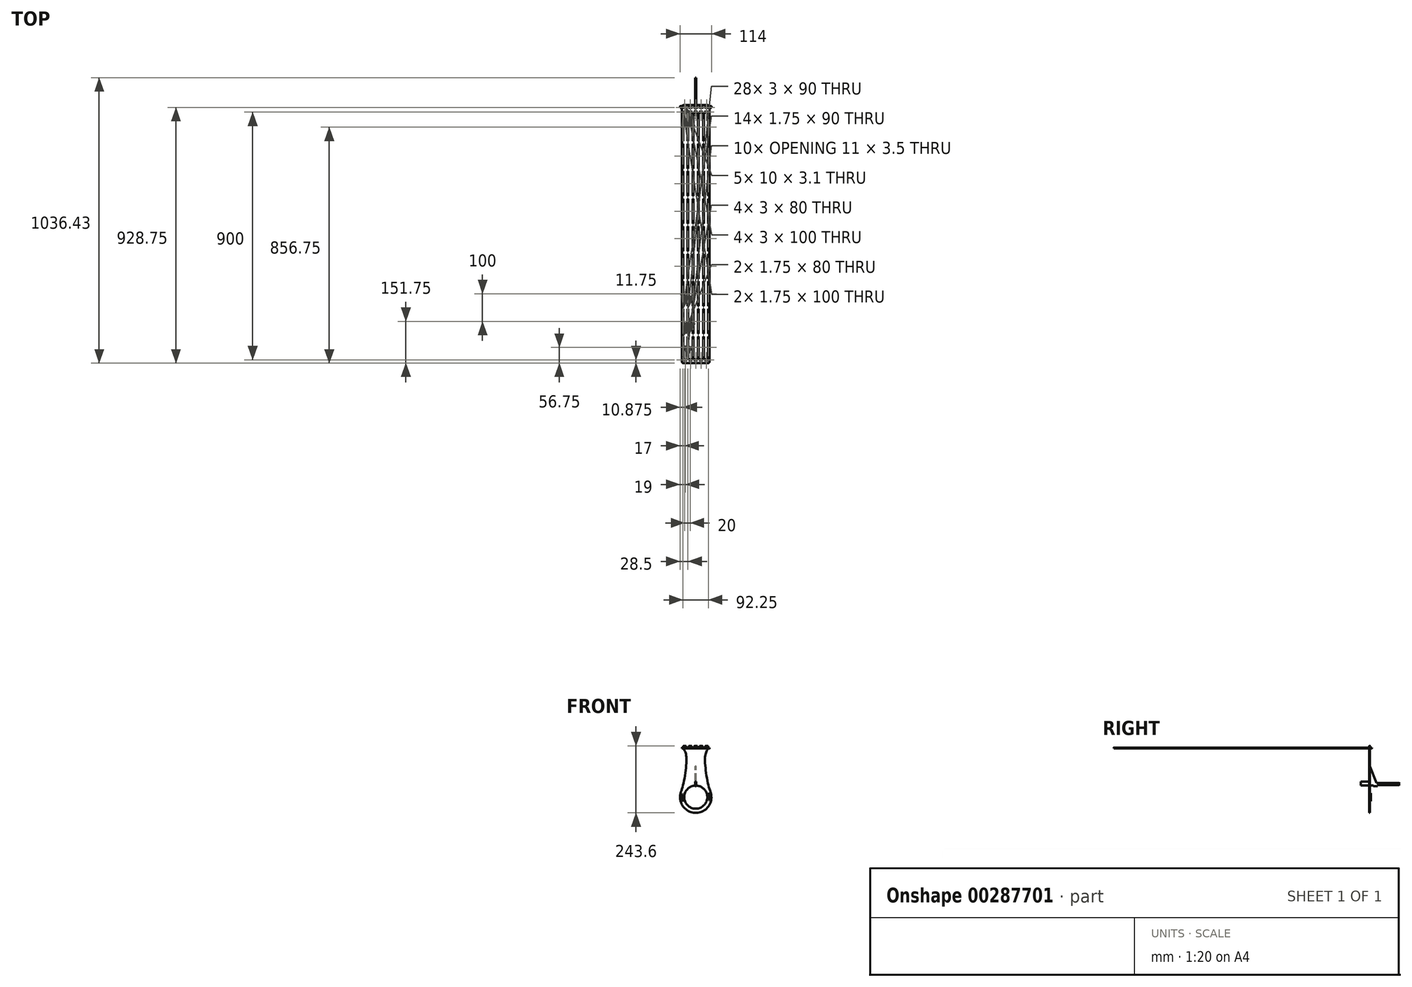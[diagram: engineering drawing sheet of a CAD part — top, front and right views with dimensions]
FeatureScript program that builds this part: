
annotation { "Feature Type Name" : "Feature", "Feature Type Description" : "" }
export const myFeature = defineFeature(function(context is Context, id is Id, definition is map)
    precondition{}
    {
        {
            var Q0;
            Q0=qCreatedBy(makeId("Top.planeOp"),FACE);
            var sketch = newSketch(context, id + "F0", { "sketchPlane" : qUnion([Q0])});
            skLineSegment(sketch, "E0.bottom", {"start": v(-45, 475) * mm, "end": v(45, 475) * mm});
            skLineSegment(sketch, "E0.top", {"start": v(-45, -475) * mm, "end": v(45, -475) * mm});
            skLineSegment(sketch, "E0.left", {"start": v(-50, 470) * mm, "end": v(-50, -456.75) * mm});
            skLineSegment(sketch, "E0.right", {"start": v(50, 470) * mm, "end": v(50, -456.75) * mm});
            skPoint(sketch, "E0.middle", {"position": v(0, 0) * mm});
            skLineSegment(sketch, "E1", {"start": v(-50, 450) * mm, "end": v(50, 450) * mm, "construction": true});
            skLineSegment(sketch, "E2", {"start": v(-50, -450) * mm, "end": v(50, -450) * mm, "construction": true});
            skLineSegment(sketch, "E3.bottom", {"start": v(-5, 451.75) * mm, "end": v(5, 451.75) * mm});
            skLineSegment(sketch, "E3.top", {"start": v(-5, 448.25) * mm, "end": v(5, 448.25) * mm});
            skLineSegment(sketch, "E3.left", {"start": v(-5.5, 451.25) * mm, "end": v(-5.5, 448.75) * mm});
            skLineSegment(sketch, "E3.right", {"start": v(5.5, 451.25) * mm, "end": v(5.5, 448.75) * mm});
            skPoint(sketch, "E3.middle", {"position": v(0, 450) * mm});
            skPoint(sketch, "E4.visualSharp", {"position": v(-5.5, 451.75) * mm});
            skArc(sketch, "E4.filletArc", {"start": v(-5, 451.75) * mm, "mid": v(-5.35, 451.6) * mm, "end": v(-5.5, 451.25) * mm});
            skPoint(sketch, "E5.visualSharp", {"position": v(-5.5, 448.25) * mm});
            skArc(sketch, "E5.filletArc", {"start": v(-5.5, 448.75) * mm, "mid": v(-5.35, 448.4) * mm, "end": v(-5, 448.25) * mm});
            skPoint(sketch, "E6.visualSharp", {"position": v(5.5, 451.75) * mm});
            skArc(sketch, "E6.filletArc", {"start": v(5.5, 451.25) * mm, "mid": v(5.35, 451.6) * mm, "end": v(5, 451.75) * mm});
            skPoint(sketch, "E7.visualSharp", {"position": v(5.5, 448.25) * mm});
            skArc(sketch, "E7.filletArc", {"start": v(5, 448.25) * mm, "mid": v(5.35, 448.4) * mm, "end": v(5.5, 448.75) * mm});
            skLineSegment(sketch, "E8.1.0.0", {"start": v(14, 451.75) * mm, "end": v(24, 451.75) * mm});
            skLineSegment(sketch, "E8.1.0.1", {"start": v(24.5, 451.25) * mm, "end": v(24.5, 448.75) * mm});
            skLineSegment(sketch, "E8.1.0.2", {"start": v(13.5, 451.25) * mm, "end": v(13.5, 448.75) * mm});
            skLineSegment(sketch, "E8.1.0.3", {"start": v(14, 448.25) * mm, "end": v(24, 448.25) * mm});
            skPoint(sketch, "E8.1.0.4", {"position": v(13.5, 448.25) * mm});
            skPoint(sketch, "E8.1.0.5", {"position": v(24.5, 451.75) * mm});
            skPoint(sketch, "E8.1.0.6", {"position": v(19, 450) * mm});
            skPoint(sketch, "E8.1.0.7", {"position": v(24.5, 448.25) * mm});
            skPoint(sketch, "E8.1.0.8", {"position": v(13.5, 451.75) * mm});
            skArc(sketch, "E8.1.0.9", {"start": v(24, 448.25) * mm, "mid": v(24.35, 448.4) * mm, "end": v(24.5, 448.75) * mm});
            skArc(sketch, "E8.1.0.10", {"start": v(14, 451.75) * mm, "mid": v(13.65, 451.6) * mm, "end": v(13.5, 451.25) * mm});
            skArc(sketch, "E8.1.0.11", {"start": v(13.5, 448.75) * mm, "mid": v(13.65, 448.4) * mm, "end": v(14, 448.25) * mm});
            skArc(sketch, "E8.1.0.12", {"start": v(24.5, 451.25) * mm, "mid": v(24.35, 451.6) * mm, "end": v(24, 451.75) * mm});
            skLineSegment(sketch, "E8.2.0.0", {"start": v(33, 451.75) * mm, "end": v(43, 451.75) * mm});
            skLineSegment(sketch, "E8.2.0.1", {"start": v(43.5, 451.25) * mm, "end": v(43.5, 448.75) * mm});
            skLineSegment(sketch, "E8.2.0.2", {"start": v(32.5, 451.25) * mm, "end": v(32.5, 448.75) * mm});
            skLineSegment(sketch, "E8.2.0.3", {"start": v(33, 448.25) * mm, "end": v(43, 448.25) * mm});
            skPoint(sketch, "E8.2.0.4", {"position": v(32.5, 448.25) * mm});
            skPoint(sketch, "E8.2.0.5", {"position": v(43.5, 451.75) * mm});
            skPoint(sketch, "E8.2.0.6", {"position": v(38, 450) * mm});
            skPoint(sketch, "E8.2.0.7", {"position": v(43.5, 448.25) * mm});
            skPoint(sketch, "E8.2.0.8", {"position": v(32.5, 451.75) * mm});
            skArc(sketch, "E8.2.0.9", {"start": v(43, 448.25) * mm, "mid": v(43.35, 448.4) * mm, "end": v(43.5, 448.75) * mm});
            skArc(sketch, "E8.2.0.10", {"start": v(33, 451.75) * mm, "mid": v(32.65, 451.6) * mm, "end": v(32.5, 451.25) * mm});
            skArc(sketch, "E8.2.0.11", {"start": v(32.5, 448.75) * mm, "mid": v(32.65, 448.4) * mm, "end": v(33, 448.25) * mm});
            skArc(sketch, "E8.2.0.12", {"start": v(43.5, 451.25) * mm, "mid": v(43.35, 451.6) * mm, "end": v(43, 451.75) * mm});
            skLineSegment(sketch, "E8.direction1", {"start": v(-5.5, 448.25) * mm, "end": v(13.5, 448.25) * mm, "construction": true});
            skPoint(sketch, "E9.1.0.0", {"position": v(-24.5, 448.25) * mm});
            skPoint(sketch, "E9.1.0.1", {"position": v(-13.5, 448.25) * mm});
            skPoint(sketch, "E9.1.0.2", {"position": v(-19, 450) * mm});
            skPoint(sketch, "E9.1.0.3", {"position": v(-13.5, 451.75) * mm});
            skPoint(sketch, "E9.1.0.4", {"position": v(-24.5, 451.75) * mm});
            skLineSegment(sketch, "E9.1.0.5", {"start": v(-24, 451.75) * mm, "end": v(-14, 451.75) * mm});
            skLineSegment(sketch, "E9.1.0.6", {"start": v(-24, 448.25) * mm, "end": v(-14, 448.25) * mm});
            skLineSegment(sketch, "E9.1.0.7", {"start": v(-24.5, 451.25) * mm, "end": v(-24.5, 448.75) * mm});
            skLineSegment(sketch, "E9.1.0.8", {"start": v(-13.5, 451.25) * mm, "end": v(-13.5, 448.75) * mm});
            skArc(sketch, "E9.1.0.9", {"start": v(-13.5, 451.25) * mm, "mid": v(-13.65, 451.6) * mm, "end": v(-14, 451.75) * mm});
            skArc(sketch, "E9.1.0.10", {"start": v(-24.5, 448.75) * mm, "mid": v(-24.35, 448.4) * mm, "end": v(-24, 448.25) * mm});
            skArc(sketch, "E9.1.0.11", {"start": v(-24, 451.75) * mm, "mid": v(-24.35, 451.6) * mm, "end": v(-24.5, 451.25) * mm});
            skArc(sketch, "E9.1.0.12", {"start": v(-14, 448.25) * mm, "mid": v(-13.65, 448.4) * mm, "end": v(-13.5, 448.75) * mm});
            skPoint(sketch, "E9.2.0.0", {"position": v(-43.5, 448.25) * mm});
            skPoint(sketch, "E9.2.0.1", {"position": v(-32.5, 448.25) * mm});
            skPoint(sketch, "E9.2.0.2", {"position": v(-38, 450) * mm});
            skPoint(sketch, "E9.2.0.3", {"position": v(-32.5, 451.75) * mm});
            skPoint(sketch, "E9.2.0.4", {"position": v(-43.5, 451.75) * mm});
            skLineSegment(sketch, "E9.2.0.5", {"start": v(-43, 451.75) * mm, "end": v(-33, 451.75) * mm});
            skLineSegment(sketch, "E9.2.0.6", {"start": v(-43, 448.25) * mm, "end": v(-33, 448.25) * mm});
            skLineSegment(sketch, "E9.2.0.7", {"start": v(-43.5, 451.25) * mm, "end": v(-43.5, 448.75) * mm});
            skLineSegment(sketch, "E9.2.0.8", {"start": v(-32.5, 451.25) * mm, "end": v(-32.5, 448.75) * mm});
            skArc(sketch, "E9.2.0.9", {"start": v(-32.5, 451.25) * mm, "mid": v(-32.65, 451.6) * mm, "end": v(-33, 451.75) * mm});
            skArc(sketch, "E9.2.0.10", {"start": v(-43.5, 448.75) * mm, "mid": v(-43.35, 448.4) * mm, "end": v(-43, 448.25) * mm});
            skArc(sketch, "E9.2.0.11", {"start": v(-43, 451.75) * mm, "mid": v(-43.35, 451.6) * mm, "end": v(-43.5, 451.25) * mm});
            skArc(sketch, "E9.2.0.12", {"start": v(-33, 448.25) * mm, "mid": v(-32.65, 448.4) * mm, "end": v(-32.5, 448.75) * mm});
            skLineSegment(sketch, "E9.direction1", {"start": v(-5.5, 448.25) * mm, "end": v(-24.5, 448.25) * mm, "construction": true});
            skLineSegment(sketch, "E10", {"start": v(-50, 467) * mm, "end": v(50, 467) * mm, "construction": true});
            skLineSegment(sketch, "E11.bottom", {"start": v(-5, 468.55) * mm, "end": v(5, 468.55) * mm});
            skLineSegment(sketch, "E11.top", {"start": v(-5, 465.45) * mm, "end": v(5, 465.45) * mm});
            skLineSegment(sketch, "E11.left", {"start": v(-5, 468.55) * mm, "end": v(-5, 465.45) * mm});
            skLineSegment(sketch, "E11.right", {"start": v(5, 468.55) * mm, "end": v(5, 465.45) * mm});
            skPoint(sketch, "E11.middle", {"position": v(0, 467) * mm});
            skPoint(sketch, "E12.visualSharp", {"position": v(-50, 475) * mm});
            skArc(sketch, "E12.filletArc", {"start": v(-45, 475) * mm, "mid": v(-48.54, 473.54) * mm, "end": v(-50, 470) * mm});
            skPoint(sketch, "E13.visualSharp", {"position": v(50, 475) * mm});
            skArc(sketch, "E13.filletArc", {"start": v(50, 470) * mm, "mid": v(48.54, 473.54) * mm, "end": v(45, 475) * mm});
            skPoint(sketch, "E14.visualSharp", {"position": v(-50, -475) * mm});
            skArc(sketch, "E14.filletArc", {"start": v(-50, -470) * mm, "mid": v(-48.54, -473.54) * mm, "end": v(-45, -475) * mm});
            skPoint(sketch, "E15.visualSharp", {"position": v(50, -475) * mm});
            skArc(sketch, "E15.filletArc", {"start": v(45, -475) * mm, "mid": v(48.54, -473.54) * mm, "end": v(50, -470) * mm});
            skPoint(sketch, "E16.1.0.0", {"position": v(20, 467) * mm});
            skLineSegment(sketch, "E16.1.0.1", {"start": v(25, 468.55) * mm, "end": v(25, 465.45) * mm});
            skLineSegment(sketch, "E16.1.0.2", {"start": v(15, 468.55) * mm, "end": v(25, 468.55) * mm});
            skLineSegment(sketch, "E16.1.0.3", {"start": v(15, 468.55) * mm, "end": v(15, 465.45) * mm});
            skLineSegment(sketch, "E16.1.0.4", {"start": v(15, 465.45) * mm, "end": v(25, 465.45) * mm});
            skPoint(sketch, "E16.2.0.0", {"position": v(40, 467) * mm});
            skLineSegment(sketch, "E16.2.0.1", {"start": v(45, 468.55) * mm, "end": v(45, 465.45) * mm});
            skLineSegment(sketch, "E16.2.0.2", {"start": v(35, 468.55) * mm, "end": v(45, 468.55) * mm});
            skLineSegment(sketch, "E16.2.0.3", {"start": v(35, 468.55) * mm, "end": v(35, 465.45) * mm});
            skLineSegment(sketch, "E16.2.0.4", {"start": v(35, 465.45) * mm, "end": v(45, 465.45) * mm});
            skLineSegment(sketch, "E16.direction1", {"start": v(-5, 465.45) * mm, "end": v(15, 465.45) * mm, "construction": true});
            skLineSegment(sketch, "E17.1.0.0", {"start": v(-15, 468.55) * mm, "end": v(-15, 465.45) * mm});
            skLineSegment(sketch, "E17.1.0.1", {"start": v(-25, 468.55) * mm, "end": v(-25, 465.45) * mm});
            skPoint(sketch, "E17.1.0.2", {"position": v(-20, 467) * mm});
            skLineSegment(sketch, "E17.1.0.3", {"start": v(-25, 465.45) * mm, "end": v(-15, 465.45) * mm});
            skLineSegment(sketch, "E17.1.0.4", {"start": v(-25, 468.55) * mm, "end": v(-15, 468.55) * mm});
            skLineSegment(sketch, "E17.2.0.0", {"start": v(-35, 468.55) * mm, "end": v(-35, 465.45) * mm});
            skLineSegment(sketch, "E17.2.0.1", {"start": v(-45, 468.55) * mm, "end": v(-45, 465.45) * mm});
            skPoint(sketch, "E17.2.0.2", {"position": v(-40, 467) * mm});
            skLineSegment(sketch, "E17.2.0.3", {"start": v(-45, 465.45) * mm, "end": v(-35, 465.45) * mm});
            skLineSegment(sketch, "E17.2.0.4", {"start": v(-45, 468.55) * mm, "end": v(-35, 468.55) * mm});
            skLineSegment(sketch, "E17.direction1", {"start": v(-5, 465.45) * mm, "end": v(-25, 465.45) * mm, "construction": true});
            skArc(sketch, "E18.MirrorCS", {"start": v(-5.5, -448.75) * mm, "mid": v(-5.35, -448.4) * mm, "end": v(-5, -448.25) * mm});
            skArc(sketch, "E19.MirrorCS", {"start": v(24, -448.25) * mm, "mid": v(24.35, -448.4) * mm, "end": v(24.5, -448.75) * mm});
            skArc(sketch, "E20.MirrorCS", {"start": v(5.5, -451.25) * mm, "mid": v(5.35, -451.6) * mm, "end": v(5, -451.75) * mm});
            skArc(sketch, "E21.MirrorCS", {"start": v(-5, -451.75) * mm, "mid": v(-5.35, -451.6) * mm, "end": v(-5.5, -451.25) * mm});
            skArc(sketch, "E22.MirrorCS", {"start": v(5, -448.25) * mm, "mid": v(5.35, -448.4) * mm, "end": v(5.5, -448.75) * mm});
            skArc(sketch, "E23.MirrorCS", {"start": v(-14, -448.25) * mm, "mid": v(-13.65, -448.4) * mm, "end": v(-13.5, -448.75) * mm});
            skArc(sketch, "E24.MirrorCS", {"start": v(-24, -451.75) * mm, "mid": v(-24.35, -451.6) * mm, "end": v(-24.5, -451.25) * mm});
            skArc(sketch, "E25.MirrorCS", {"start": v(-33, -448.25) * mm, "mid": v(-32.65, -448.4) * mm, "end": v(-32.5, -448.75) * mm});
            skArc(sketch, "E26.MirrorCS", {"start": v(24.5, -451.25) * mm, "mid": v(24.35, -451.6) * mm, "end": v(24, -451.75) * mm});
            skArc(sketch, "E27.MirrorCS", {"start": v(32.5, -448.75) * mm, "mid": v(32.65, -448.4) * mm, "end": v(33, -448.25) * mm});
            skArc(sketch, "E28.MirrorCS", {"start": v(-43.5, -448.75) * mm, "mid": v(-43.35, -448.4) * mm, "end": v(-43, -448.25) * mm});
            skArc(sketch, "E29.MirrorCS", {"start": v(-24.5, -448.75) * mm, "mid": v(-24.35, -448.4) * mm, "end": v(-24, -448.25) * mm});
            skArc(sketch, "E30.MirrorCS", {"start": v(43.5, -451.25) * mm, "mid": v(43.35, -451.6) * mm, "end": v(43, -451.75) * mm});
            skArc(sketch, "E31.MirrorCS", {"start": v(-43, -451.75) * mm, "mid": v(-43.35, -451.6) * mm, "end": v(-43.5, -451.25) * mm});
            skArc(sketch, "E32.MirrorCS", {"start": v(13.5, -448.75) * mm, "mid": v(13.65, -448.4) * mm, "end": v(14, -448.25) * mm});
            skArc(sketch, "E33.MirrorCS", {"start": v(33, -451.75) * mm, "mid": v(32.65, -451.6) * mm, "end": v(32.5, -451.25) * mm});
            skArc(sketch, "E34.MirrorCS", {"start": v(-32.5, -451.25) * mm, "mid": v(-32.65, -451.6) * mm, "end": v(-33, -451.75) * mm});
            skArc(sketch, "E35.MirrorCS", {"start": v(-13.5, -451.25) * mm, "mid": v(-13.65, -451.6) * mm, "end": v(-14, -451.75) * mm});
            skArc(sketch, "E36.MirrorCS", {"start": v(14, -451.75) * mm, "mid": v(13.65, -451.6) * mm, "end": v(13.5, -451.25) * mm});
            skArc(sketch, "E37.MirrorCS", {"start": v(43, -448.25) * mm, "mid": v(43.35, -448.4) * mm, "end": v(43.5, -448.75) * mm});
            skLineSegment(sketch, "E38.MirrorCS", {"start": v(-13.5, -451.25) * mm, "end": v(-13.5, -448.75) * mm});
            skLineSegment(sketch, "E39.MirrorCS", {"start": v(-24, -448.25) * mm, "end": v(-14, -448.25) * mm});
            skLineSegment(sketch, "E40.MirrorCS", {"start": v(-5, -448.25) * mm, "end": v(5, -448.25) * mm});
            skPoint(sketch, "E41.MirrorP", {"position": v(32.5, -448.25) * mm});
            skLineSegment(sketch, "E42.MirrorCS", {"start": v(33, -448.25) * mm, "end": v(43, -448.25) * mm});
            skLineSegment(sketch, "E43.MirrorCS", {"start": v(-43.5, -451.25) * mm, "end": v(-43.5, -448.75) * mm});
            skPoint(sketch, "E44.MirrorP", {"position": v(19, -450) * mm});
            skPoint(sketch, "E45.MirrorP", {"position": v(-24.5, -448.25) * mm});
            skPoint(sketch, "E46.MirrorP", {"position": v(-5.5, -451.75) * mm});
            skLineSegment(sketch, "E47.MirrorCS", {"start": v(-24.5, -451.25) * mm, "end": v(-24.5, -448.75) * mm});
            skLineSegment(sketch, "E48.MirrorCS", {"start": v(14, -448.25) * mm, "end": v(24, -448.25) * mm});
            skPoint(sketch, "E49.MirrorP", {"position": v(24.5, -451.75) * mm});
            skLineSegment(sketch, "E50.MirrorCS", {"start": v(32.5, -451.25) * mm, "end": v(32.5, -448.75) * mm});
            skLineSegment(sketch, "E51.MirrorCS", {"start": v(-43, -448.25) * mm, "end": v(-33, -448.25) * mm});
            skLineSegment(sketch, "E52.MirrorCS", {"start": v(13.5, -451.25) * mm, "end": v(13.5, -448.75) * mm});
            skPoint(sketch, "E53.MirrorP", {"position": v(13.5, -448.25) * mm});
            skLineSegment(sketch, "E54.MirrorCS", {"start": v(43.5, -451.25) * mm, "end": v(43.5, -448.75) * mm});
            skLineSegment(sketch, "E55.MirrorCS", {"start": v(-43, -451.75) * mm, "end": v(-33, -451.75) * mm});
            skPoint(sketch, "E56.MirrorP", {"position": v(0, -450) * mm});
            skLineSegment(sketch, "E57.MirrorCS", {"start": v(5.5, -451.25) * mm, "end": v(5.5, -448.75) * mm});
            skLineSegment(sketch, "E58.MirrorCS", {"start": v(-5.5, -451.25) * mm, "end": v(-5.5, -448.75) * mm});
            skLineSegment(sketch, "E59.MirrorCS", {"start": v(-5, -451.75) * mm, "end": v(5, -451.75) * mm});
            skLineSegment(sketch, "E60.MirrorCS", {"start": v(24.5, -451.25) * mm, "end": v(24.5, -448.75) * mm});
            skLineSegment(sketch, "E61.MirrorCS", {"start": v(14, -451.75) * mm, "end": v(24, -451.75) * mm});
            skLineSegment(sketch, "E62.MirrorCS", {"start": v(-24, -451.75) * mm, "end": v(-14, -451.75) * mm});
            skLineSegment(sketch, "E63.MirrorCS", {"start": v(-5.5, -448.25) * mm, "end": v(-24.5, -448.25) * mm, "construction": true});
            skLineSegment(sketch, "E64.MirrorCS", {"start": v(33, -451.75) * mm, "end": v(43, -451.75) * mm});
            skPoint(sketch, "E65.MirrorP", {"position": v(-24.5, -451.75) * mm});
            skPoint(sketch, "E66.MirrorP", {"position": v(-43.5, -451.75) * mm});
            skPoint(sketch, "E67.MirrorP", {"position": v(-32.5, -448.25) * mm});
            skPoint(sketch, "E68.MirrorP", {"position": v(5.5, -451.75) * mm});
            skPoint(sketch, "E69.MirrorP", {"position": v(43.5, -448.25) * mm});
            skLineSegment(sketch, "E70.MirrorCS", {"start": v(-5.5, -448.25) * mm, "end": v(13.5, -448.25) * mm, "construction": true});
            skPoint(sketch, "E71.MirrorP", {"position": v(5.5, -448.25) * mm});
            skPoint(sketch, "E72.MirrorP", {"position": v(-13.5, -451.75) * mm});
            skPoint(sketch, "E73.MirrorP", {"position": v(-32.5, -451.75) * mm});
            skPoint(sketch, "E74.MirrorP", {"position": v(-43.5, -448.25) * mm});
            skPoint(sketch, "E75.MirrorP", {"position": v(38, -450) * mm});
            skPoint(sketch, "E76.MirrorP", {"position": v(13.5, -451.75) * mm});
            skPoint(sketch, "E77.MirrorP", {"position": v(32.5, -451.75) * mm});
            skPoint(sketch, "E78.MirrorP", {"position": v(-19, -450) * mm});
            skPoint(sketch, "E79.MirrorP", {"position": v(-38, -450) * mm});
            skPoint(sketch, "E80.MirrorP", {"position": v(-5.5, -448.25) * mm});
            skPoint(sketch, "E81.MirrorP", {"position": v(43.5, -451.75) * mm});
            skLineSegment(sketch, "E82.MirrorCS", {"start": v(-32.5, -451.25) * mm, "end": v(-32.5, -448.75) * mm});
            skPoint(sketch, "E83.MirrorP", {"position": v(24.5, -448.25) * mm});
            skPoint(sketch, "E84.MirrorP", {"position": v(-13.5, -448.25) * mm});
            skLineSegment(sketch, "E85", {"start": v(-45, -461.75) * mm, "end": v(45, -461.75) * mm});
            skArc(sketch, "E86.filletArc", {"start": v(-50, -456.75) * mm, "mid": v(-48.54, -460.29) * mm, "end": v(-45, -461.75) * mm});
            skArc(sketch, "E87.filletArc", {"start": v(45, -461.75) * mm, "mid": v(48.54, -460.29) * mm, "end": v(50, -456.75) * mm});
            skLineSegment(sketch, "E88.bottom", {"start": v(-30, 445) * mm, "end": v(-27, 445) * mm});
            skLineSegment(sketch, "E88.top", {"start": v(-30, -445) * mm, "end": v(-27, -445) * mm});
            skLineSegment(sketch, "E88.left", {"start": v(-30, 445) * mm, "end": v(-30, -445) * mm});
            skLineSegment(sketch, "E88.right", {"start": v(-27, 445) * mm, "end": v(-27, -445) * mm});
            skLineSegment(sketch, "E89.1.0.0", {"start": v(-11, 445) * mm, "end": v(-11, -445) * mm});
            skLineSegment(sketch, "E89.1.0.1", {"start": v(-11, 445) * mm, "end": v(-8, 445) * mm});
            skLineSegment(sketch, "E89.1.0.2", {"start": v(-8, 445) * mm, "end": v(-8, -445) * mm});
            skLineSegment(sketch, "E89.1.0.3", {"start": v(-11, -445) * mm, "end": v(-8, -445) * mm});
            skLineSegment(sketch, "E89.2.0.0", {"start": v(8, 445) * mm, "end": v(8, -445) * mm});
            skLineSegment(sketch, "E89.2.0.1", {"start": v(8, 445) * mm, "end": v(11, 445) * mm});
            skLineSegment(sketch, "E89.2.0.2", {"start": v(11, 445) * mm, "end": v(11, -445) * mm});
            skLineSegment(sketch, "E89.2.0.3", {"start": v(8, -445) * mm, "end": v(11, -445) * mm});
            skLineSegment(sketch, "E89.3.0.0", {"start": v(27, 445) * mm, "end": v(27, -445) * mm});
            skLineSegment(sketch, "E89.3.0.1", {"start": v(27, 445) * mm, "end": v(30, 445) * mm});
            skLineSegment(sketch, "E89.3.0.2", {"start": v(30, 445) * mm, "end": v(30, -445) * mm});
            skLineSegment(sketch, "E89.3.0.3", {"start": v(27, -445) * mm, "end": v(30, -445) * mm});
            skLineSegment(sketch, "E89.direction1", {"start": v(-30, -445) * mm, "end": v(-11, -445) * mm, "construction": true});
            skLineSegment(sketch, "E90", {"start": v(-47, 445) * mm, "end": v(-45.25, 445) * mm});
            skLineSegment(sketch, "E91", {"start": v(-45.25, 445) * mm, "end": v(-45.25, -445) * mm});
            skLineSegment(sketch, "E92", {"start": v(-45.25, -445) * mm, "end": v(-47, -445) * mm});
            skLineSegment(sketch, "E93", {"start": v(-47, -445) * mm, "end": v(-47, 445) * mm});
            skLineSegment(sketch, "E94.MirrorCS", {"start": v(47, 445) * mm, "end": v(45.25, 445) * mm});
            skLineSegment(sketch, "E95.MirrorCS", {"start": v(47, -445) * mm, "end": v(47, 445) * mm});
            skLineSegment(sketch, "E96.MirrorCS", {"start": v(45.25, 445) * mm, "end": v(45.25, -445) * mm});
            skLineSegment(sketch, "E97.MirrorCS", {"start": v(45.25, -445) * mm, "end": v(47, -445) * mm});
            skLineSegment(sketch, "E98", {"start": v(-47, 345) * mm, "end": v(-45.25, 345) * mm});
            skLineSegment(sketch, "E99", {"start": v(-30, 345) * mm, "end": v(-27, 345) * mm});
            skLineSegment(sketch, "E100", {"start": v(-11, 345) * mm, "end": v(-8, 345) * mm});
            skLineSegment(sketch, "E101", {"start": v(8, 345) * mm, "end": v(11, 345) * mm});
            skLineSegment(sketch, "E102", {"start": v(27, 345) * mm, "end": v(30, 345) * mm});
            skLineSegment(sketch, "E103", {"start": v(45.25, 345) * mm, "end": v(47, 345) * mm});
            skLineSegment(sketch, "E104", {"start": v(-47, 335) * mm, "end": v(-45.25, 335) * mm});
            skLineSegment(sketch, "E105", {"start": v(-30, 335) * mm, "end": v(-27, 335) * mm});
            skLineSegment(sketch, "E106", {"start": v(-11, 335) * mm, "end": v(-8, 335) * mm});
            skLineSegment(sketch, "E107", {"start": v(8, 335) * mm, "end": v(11, 335) * mm});
            skLineSegment(sketch, "E108", {"start": v(27, 335) * mm, "end": v(30, 335) * mm});
            skLineSegment(sketch, "E109", {"start": v(45.25, 335) * mm, "end": v(47, 335) * mm});
            skLineSegment(sketch, "E110.0.1.0", {"start": v(-47, 245) * mm, "end": v(-45.25, 245) * mm});
            skLineSegment(sketch, "E110.0.1.1", {"start": v(-47, 235) * mm, "end": v(-45.25, 235) * mm});
            skLineSegment(sketch, "E110.0.1.2", {"start": v(-30, 245) * mm, "end": v(-27, 245) * mm});
            skLineSegment(sketch, "E110.0.1.3", {"start": v(-30, 235) * mm, "end": v(-27, 235) * mm});
            skLineSegment(sketch, "E110.0.1.4", {"start": v(-11, 245) * mm, "end": v(-8, 245) * mm});
            skLineSegment(sketch, "E110.0.1.5", {"start": v(-11, 235) * mm, "end": v(-8, 235) * mm});
            skLineSegment(sketch, "E110.0.1.6", {"start": v(8, 245) * mm, "end": v(11, 245) * mm});
            skLineSegment(sketch, "E110.0.1.7", {"start": v(8, 235) * mm, "end": v(11, 235) * mm});
            skLineSegment(sketch, "E110.0.1.8", {"start": v(27, 245) * mm, "end": v(30, 245) * mm});
            skLineSegment(sketch, "E110.0.1.9", {"start": v(27, 235) * mm, "end": v(30, 235) * mm});
            skLineSegment(sketch, "E110.0.1.10", {"start": v(45.25, 245) * mm, "end": v(47, 245) * mm});
            skLineSegment(sketch, "E110.0.1.11", {"start": v(45.25, 235) * mm, "end": v(47, 235) * mm});
            skLineSegment(sketch, "E110.0.2.0", {"start": v(-47, 145) * mm, "end": v(-45.25, 145) * mm});
            skLineSegment(sketch, "E110.0.2.1", {"start": v(-47, 135) * mm, "end": v(-45.25, 135) * mm});
            skLineSegment(sketch, "E110.0.2.2", {"start": v(-30, 145) * mm, "end": v(-27, 145) * mm});
            skLineSegment(sketch, "E110.0.2.3", {"start": v(-30, 135) * mm, "end": v(-27, 135) * mm});
            skLineSegment(sketch, "E110.0.2.4", {"start": v(-11, 145) * mm, "end": v(-8, 145) * mm});
            skLineSegment(sketch, "E110.0.2.5", {"start": v(-11, 135) * mm, "end": v(-8, 135) * mm});
            skLineSegment(sketch, "E110.0.2.6", {"start": v(8, 145) * mm, "end": v(11, 145) * mm});
            skLineSegment(sketch, "E110.0.2.7", {"start": v(8, 135) * mm, "end": v(11, 135) * mm});
            skLineSegment(sketch, "E110.0.2.8", {"start": v(27, 145) * mm, "end": v(30, 145) * mm});
            skLineSegment(sketch, "E110.0.2.9", {"start": v(27, 135) * mm, "end": v(30, 135) * mm});
            skLineSegment(sketch, "E110.0.2.10", {"start": v(45.25, 145) * mm, "end": v(47, 145) * mm});
            skLineSegment(sketch, "E110.0.2.11", {"start": v(45.25, 135) * mm, "end": v(47, 135) * mm});
            skLineSegment(sketch, "E110.0.3.0", {"start": v(-47, 45) * mm, "end": v(-45.25, 45) * mm});
            skLineSegment(sketch, "E110.0.3.1", {"start": v(-47, 35) * mm, "end": v(-45.25, 35) * mm});
            skLineSegment(sketch, "E110.0.3.2", {"start": v(-30, 45) * mm, "end": v(-27, 45) * mm});
            skLineSegment(sketch, "E110.0.3.3", {"start": v(-30, 35) * mm, "end": v(-27, 35) * mm});
            skLineSegment(sketch, "E110.0.3.4", {"start": v(-11, 45) * mm, "end": v(-8, 45) * mm});
            skLineSegment(sketch, "E110.0.3.5", {"start": v(-11, 35) * mm, "end": v(-8, 35) * mm});
            skLineSegment(sketch, "E110.0.3.6", {"start": v(8, 45) * mm, "end": v(11, 45) * mm});
            skLineSegment(sketch, "E110.0.3.7", {"start": v(8, 35) * mm, "end": v(11, 35) * mm});
            skLineSegment(sketch, "E110.0.3.8", {"start": v(27, 45) * mm, "end": v(30, 45) * mm});
            skLineSegment(sketch, "E110.0.3.9", {"start": v(27, 35) * mm, "end": v(30, 35) * mm});
            skLineSegment(sketch, "E110.0.3.10", {"start": v(45.25, 45) * mm, "end": v(47, 45) * mm});
            skLineSegment(sketch, "E110.0.3.11", {"start": v(45.25, 35) * mm, "end": v(47, 35) * mm});
            skLineSegment(sketch, "E110.0.4.0", {"start": v(-47, -55) * mm, "end": v(-45.25, -55) * mm});
            skLineSegment(sketch, "E110.0.4.1", {"start": v(-47, -65) * mm, "end": v(-45.25, -65) * mm});
            skLineSegment(sketch, "E110.0.4.2", {"start": v(-30, -55) * mm, "end": v(-27, -55) * mm});
            skLineSegment(sketch, "E110.0.4.3", {"start": v(-30, -65) * mm, "end": v(-27, -65) * mm});
            skLineSegment(sketch, "E110.0.4.4", {"start": v(-11, -55) * mm, "end": v(-8, -55) * mm});
            skLineSegment(sketch, "E110.0.4.5", {"start": v(-11, -65) * mm, "end": v(-8, -65) * mm});
            skLineSegment(sketch, "E110.0.4.6", {"start": v(8, -55) * mm, "end": v(11, -55) * mm});
            skLineSegment(sketch, "E110.0.4.7", {"start": v(8, -65) * mm, "end": v(11, -65) * mm});
            skLineSegment(sketch, "E110.0.4.8", {"start": v(27, -55) * mm, "end": v(30, -55) * mm});
            skLineSegment(sketch, "E110.0.4.9", {"start": v(27, -65) * mm, "end": v(30, -65) * mm});
            skLineSegment(sketch, "E110.0.4.10", {"start": v(45.25, -55) * mm, "end": v(47, -55) * mm});
            skLineSegment(sketch, "E110.0.4.11", {"start": v(45.25, -65) * mm, "end": v(47, -65) * mm});
            skLineSegment(sketch, "E110.0.5.0", {"start": v(-47, -155) * mm, "end": v(-45.25, -155) * mm});
            skLineSegment(sketch, "E110.0.5.1", {"start": v(-47, -165) * mm, "end": v(-45.25, -165) * mm});
            skLineSegment(sketch, "E110.0.5.2", {"start": v(-30, -155) * mm, "end": v(-27, -155) * mm});
            skLineSegment(sketch, "E110.0.5.3", {"start": v(-30, -165) * mm, "end": v(-27, -165) * mm});
            skLineSegment(sketch, "E110.0.5.4", {"start": v(-11, -155) * mm, "end": v(-8, -155) * mm});
            skLineSegment(sketch, "E110.0.5.5", {"start": v(-11, -165) * mm, "end": v(-8, -165) * mm});
            skLineSegment(sketch, "E110.0.5.6", {"start": v(8, -155) * mm, "end": v(11, -155) * mm});
            skLineSegment(sketch, "E110.0.5.7", {"start": v(8, -165) * mm, "end": v(11, -165) * mm});
            skLineSegment(sketch, "E110.0.5.8", {"start": v(27, -155) * mm, "end": v(30, -155) * mm});
            skLineSegment(sketch, "E110.0.5.9", {"start": v(27, -165) * mm, "end": v(30, -165) * mm});
            skLineSegment(sketch, "E110.0.5.10", {"start": v(45.25, -155) * mm, "end": v(47, -155) * mm});
            skLineSegment(sketch, "E110.0.5.11", {"start": v(45.25, -165) * mm, "end": v(47, -165) * mm});
            skLineSegment(sketch, "E110.0.6.0", {"start": v(-47, -255) * mm, "end": v(-45.25, -255) * mm});
            skLineSegment(sketch, "E110.0.6.1", {"start": v(-47, -265) * mm, "end": v(-45.25, -265) * mm});
            skLineSegment(sketch, "E110.0.6.2", {"start": v(-30, -255) * mm, "end": v(-27, -255) * mm});
            skLineSegment(sketch, "E110.0.6.3", {"start": v(-30, -265) * mm, "end": v(-27, -265) * mm});
            skLineSegment(sketch, "E110.0.6.4", {"start": v(-11, -255) * mm, "end": v(-8, -255) * mm});
            skLineSegment(sketch, "E110.0.6.5", {"start": v(-11, -265) * mm, "end": v(-8, -265) * mm});
            skLineSegment(sketch, "E110.0.6.6", {"start": v(8, -255) * mm, "end": v(11, -255) * mm});
            skLineSegment(sketch, "E110.0.6.7", {"start": v(8, -265) * mm, "end": v(11, -265) * mm});
            skLineSegment(sketch, "E110.0.6.8", {"start": v(27, -255) * mm, "end": v(30, -255) * mm});
            skLineSegment(sketch, "E110.0.6.9", {"start": v(27, -265) * mm, "end": v(30, -265) * mm});
            skLineSegment(sketch, "E110.0.6.10", {"start": v(45.25, -255) * mm, "end": v(47, -255) * mm});
            skLineSegment(sketch, "E110.0.6.11", {"start": v(45.25, -265) * mm, "end": v(47, -265) * mm});
            skLineSegment(sketch, "E110.0.7.0", {"start": v(-47, -355) * mm, "end": v(-45.25, -355) * mm});
            skLineSegment(sketch, "E110.0.7.1", {"start": v(-47, -365) * mm, "end": v(-45.25, -365) * mm});
            skLineSegment(sketch, "E110.0.7.2", {"start": v(-30, -355) * mm, "end": v(-27, -355) * mm});
            skLineSegment(sketch, "E110.0.7.3", {"start": v(-30, -365) * mm, "end": v(-27, -365) * mm});
            skLineSegment(sketch, "E110.0.7.4", {"start": v(-11, -355) * mm, "end": v(-8, -355) * mm});
            skLineSegment(sketch, "E110.0.7.5", {"start": v(-11, -365) * mm, "end": v(-8, -365) * mm});
            skLineSegment(sketch, "E110.0.7.6", {"start": v(8, -355) * mm, "end": v(11, -355) * mm});
            skLineSegment(sketch, "E110.0.7.7", {"start": v(8, -365) * mm, "end": v(11, -365) * mm});
            skLineSegment(sketch, "E110.0.7.8", {"start": v(27, -355) * mm, "end": v(30, -355) * mm});
            skLineSegment(sketch, "E110.0.7.9", {"start": v(27, -365) * mm, "end": v(30, -365) * mm});
            skLineSegment(sketch, "E110.0.7.10", {"start": v(45.25, -355) * mm, "end": v(47, -355) * mm});
            skLineSegment(sketch, "E110.0.7.11", {"start": v(45.25, -365) * mm, "end": v(47, -365) * mm});
            skLineSegment(sketch, "E110.direction1", {"start": v(-47, 335) * mm, "end": v(-22, 335) * mm, "construction": true});
            skLineSegment(sketch, "E110.direction2", {"start": v(-47, 335) * mm, "end": v(-47, 235) * mm, "construction": true});
            skSolve(sketch);
        }
        {
            var Q0;
            Q0=sQuery(id+"F0.wireOp",EDGE,"E11.top");
            cPlane(context, id + "F1", {"entities" : qUnion([Q0]), "cplaneType" : CPlaneType.LINE_ANGLE, "offset" : 25 * mm, "angle" : 0 * degree, "width" : 150 * mm, "height" : 150 * mm});
        }
        {
            var Q0;
            Q0=qCreatedBy(id+"F1.planeOp",FACE);
            var sketch = newSketch(context, id + "F2", { "sketchPlane" : qUnion([Q0])});
            skLineSegment(sketch, "E111.0", {"start": v(5, 0) * mm, "end": v(-5, 0) * mm, "construction": true});
            skLineSegment(sketch, "E112.0", {"start": v(25, 0) * mm, "end": v(15, 0) * mm, "construction": true});
            skLineSegment(sketch, "E113.0", {"start": v(45, 0) * mm, "end": v(35, 0) * mm, "construction": true});
            skLineSegment(sketch, "E114.0", {"start": v(-15, 0) * mm, "end": v(-25, 0) * mm, "construction": true});
            skLineSegment(sketch, "E115.0", {"start": v(-35, 0) * mm, "end": v(-45, 0) * mm, "construction": true});
            skLineSegment(sketch, "E116", {"start": v(45, 0) * mm, "end": v(45, 8.6) * mm});
            skLineSegment(sketch, "E117", {"start": v(44, 9.6) * mm, "end": v(36, 9.6) * mm});
            skLineSegment(sketch, "E118", {"start": v(35, 8.6) * mm, "end": v(35, 0) * mm});
            skLineSegment(sketch, "E119", {"start": v(35, 3) * mm, "end": v(45, 3) * mm, "construction": true});
            skPoint(sketch, "E119.endSnap0", {"position": v(45, 4.8) * mm});
            skLineSegment(sketch, "E120.bottom", {"start": v(38, 3.5) * mm, "end": v(42, 3.5) * mm});
            skLineSegment(sketch, "E120.top", {"start": v(38, 6.6) * mm, "end": v(42, 6.6) * mm});
            skLineSegment(sketch, "E120.left", {"start": v(38, 3.5) * mm, "end": v(38, 6.6) * mm});
            skLineSegment(sketch, "E120.right", {"start": v(42, 3.5) * mm, "end": v(42, 6.6) * mm});
            skPoint(sketch, "E120.middle", {"position": v(40, 5.05) * mm});
            skPoint(sketch, "E120.middle.positionSnap0", {"position": v(40, 3) * mm});
            skPoint(sketch, "E120.centerSnap0", {"position": v(40, 3) * mm});
            skPoint(sketch, "E121.visualSharp", {"position": v(45, 9.6) * mm});
            skArc(sketch, "E121.filletArc", {"start": v(45, 8.6) * mm, "mid": v(44.7, 9.3) * mm, "end": v(44, 9.6) * mm});
            skPoint(sketch, "E122.visualSharp", {"position": v(35, 9.6) * mm});
            skArc(sketch, "E122.filletArc", {"start": v(36, 9.6) * mm, "mid": v(35.3, 9.3) * mm, "end": v(35, 8.6) * mm});
            skCircle(sketch, "E123", {"center": v(0, -177) * mm, "radius": 42 * mm});
            skCircle(sketch, "E124", {"center": v(0, -177) * mm, "radius": 57 * mm});
            skFitSpline(sketch, "E125", {"points": [v(45, 0) * mm, v(34.16, -28.88) * mm, v(51.88, -153.38) * mm], "startDerivative": vector(-38.23, -64.38) * mm, "endDerivative": vector(44.47, -126.95) * mm});
            skLineSegment(sketch, "E126", {"start": v(42, -177) * mm, "end": v(57, -177) * mm});
            skLineSegment(sketch, "E127", {"start": v(-42, -177) * mm, "end": v(-57, -177) * mm});
            skFitSpline(sketch, "E128.MirrorCS", {"points": [v(-45, 0) * mm, v(-34.16, -28.88) * mm, v(-51.88, -153.38) * mm], "startDerivative": vector(38.23, -64.38) * mm, "endDerivative": vector(-44.47, -126.95) * mm});
            skLineSegment(sketch, "E129.1.0.0", {"start": v(15, 3) * mm, "end": v(25, 3) * mm, "construction": true});
            skLineSegment(sketch, "E129.1.0.1", {"start": v(18, 3.5) * mm, "end": v(22, 3.5) * mm});
            skPoint(sketch, "E129.1.0.2", {"position": v(20, 3) * mm});
            skLineSegment(sketch, "E129.1.0.3", {"start": v(24, 9.6) * mm, "end": v(16, 9.6) * mm});
            skPoint(sketch, "E129.1.0.4", {"position": v(25, 4.8) * mm});
            skPoint(sketch, "E129.1.0.5", {"position": v(15, 9.6) * mm});
            skPoint(sketch, "E129.1.0.6", {"position": v(20, 5.05) * mm});
            skPoint(sketch, "E129.1.0.7", {"position": v(25, 9.6) * mm});
            skLineSegment(sketch, "E129.1.0.8", {"start": v(18, 3.5) * mm, "end": v(18, 6.6) * mm});
            skLineSegment(sketch, "E129.1.0.9", {"start": v(22, 3.5) * mm, "end": v(22, 6.6) * mm});
            skLineSegment(sketch, "E129.1.0.10", {"start": v(18, 6.6) * mm, "end": v(22, 6.6) * mm});
            skArc(sketch, "E129.1.0.11", {"start": v(16, 9.6) * mm, "mid": v(15.3, 9.3) * mm, "end": v(15, 8.6) * mm});
            skArc(sketch, "E129.1.0.12", {"start": v(25, 8.6) * mm, "mid": v(24.7, 9.3) * mm, "end": v(24, 9.6) * mm});
            skPoint(sketch, "E129.1.0.13", {"position": v(20, 3) * mm});
            skLineSegment(sketch, "E129.1.0.14", {"start": v(15, 8.6) * mm, "end": v(15, 0) * mm});
            skLineSegment(sketch, "E129.1.0.15", {"start": v(25, 0) * mm, "end": v(25, 8.6) * mm});
            skLineSegment(sketch, "E129.2.0.0", {"start": v(-5, 3) * mm, "end": v(5, 3) * mm, "construction": true});
            skLineSegment(sketch, "E129.2.0.1", {"start": v(-2, 3.5) * mm, "end": v(2, 3.5) * mm});
            skPoint(sketch, "E129.2.0.2", {"position": v(0, 3) * mm});
            skLineSegment(sketch, "E129.2.0.3", {"start": v(4, 9.6) * mm, "end": v(-4, 9.6) * mm});
            skPoint(sketch, "E129.2.0.4", {"position": v(5, 4.8) * mm});
            skPoint(sketch, "E129.2.0.5", {"position": v(-5, 9.6) * mm});
            skPoint(sketch, "E129.2.0.6", {"position": v(0, 5.05) * mm});
            skPoint(sketch, "E129.2.0.7", {"position": v(5, 9.6) * mm});
            skLineSegment(sketch, "E129.2.0.8", {"start": v(-2, 3.5) * mm, "end": v(-2, 6.6) * mm});
            skLineSegment(sketch, "E129.2.0.9", {"start": v(2, 3.5) * mm, "end": v(2, 6.6) * mm});
            skLineSegment(sketch, "E129.2.0.10", {"start": v(-2, 6.6) * mm, "end": v(2, 6.6) * mm});
            skArc(sketch, "E129.2.0.11", {"start": v(-4, 9.6) * mm, "mid": v(-4.7, 9.3) * mm, "end": v(-5, 8.6) * mm});
            skArc(sketch, "E129.2.0.12", {"start": v(5, 8.6) * mm, "mid": v(4.7, 9.3) * mm, "end": v(4, 9.6) * mm});
            skPoint(sketch, "E129.2.0.13", {"position": v(0, 3) * mm});
            skLineSegment(sketch, "E129.2.0.14", {"start": v(-5, 8.6) * mm, "end": v(-5, 0) * mm});
            skLineSegment(sketch, "E129.2.0.15", {"start": v(5, 0) * mm, "end": v(5, 8.6) * mm});
            skLineSegment(sketch, "E129.3.0.0", {"start": v(-25, 3) * mm, "end": v(-15, 3) * mm, "construction": true});
            skLineSegment(sketch, "E129.3.0.1", {"start": v(-22, 3.5) * mm, "end": v(-18, 3.5) * mm});
            skPoint(sketch, "E129.3.0.2", {"position": v(-20, 3) * mm});
            skLineSegment(sketch, "E129.3.0.3", {"start": v(-16, 9.6) * mm, "end": v(-24, 9.6) * mm});
            skPoint(sketch, "E129.3.0.4", {"position": v(-15, 4.8) * mm});
            skPoint(sketch, "E129.3.0.5", {"position": v(-25, 9.6) * mm});
            skPoint(sketch, "E129.3.0.6", {"position": v(-20, 5.05) * mm});
            skPoint(sketch, "E129.3.0.7", {"position": v(-15, 9.6) * mm});
            skLineSegment(sketch, "E129.3.0.8", {"start": v(-22, 3.5) * mm, "end": v(-22, 6.6) * mm});
            skLineSegment(sketch, "E129.3.0.9", {"start": v(-18, 3.5) * mm, "end": v(-18, 6.6) * mm});
            skLineSegment(sketch, "E129.3.0.10", {"start": v(-22, 6.6) * mm, "end": v(-18, 6.6) * mm});
            skArc(sketch, "E129.3.0.11", {"start": v(-24, 9.6) * mm, "mid": v(-24.7, 9.3) * mm, "end": v(-25, 8.6) * mm});
            skArc(sketch, "E129.3.0.12", {"start": v(-15, 8.6) * mm, "mid": v(-15.3, 9.3) * mm, "end": v(-16, 9.6) * mm});
            skPoint(sketch, "E129.3.0.13", {"position": v(-20, 3) * mm});
            skLineSegment(sketch, "E129.3.0.14", {"start": v(-25, 8.6) * mm, "end": v(-25, 0) * mm});
            skLineSegment(sketch, "E129.3.0.15", {"start": v(-15, 0) * mm, "end": v(-15, 8.6) * mm});
            skLineSegment(sketch, "E129.4.0.0", {"start": v(-45, 3) * mm, "end": v(-35, 3) * mm, "construction": true});
            skLineSegment(sketch, "E129.4.0.1", {"start": v(-42, 3.5) * mm, "end": v(-38, 3.5) * mm});
            skPoint(sketch, "E129.4.0.2", {"position": v(-40, 3) * mm});
            skLineSegment(sketch, "E129.4.0.3", {"start": v(-36, 9.6) * mm, "end": v(-44, 9.6) * mm});
            skPoint(sketch, "E129.4.0.4", {"position": v(-35, 4.8) * mm});
            skPoint(sketch, "E129.4.0.5", {"position": v(-45, 9.6) * mm});
            skPoint(sketch, "E129.4.0.6", {"position": v(-40, 5.05) * mm});
            skPoint(sketch, "E129.4.0.7", {"position": v(-35, 9.6) * mm});
            skLineSegment(sketch, "E129.4.0.8", {"start": v(-42, 3.5) * mm, "end": v(-42, 6.6) * mm});
            skLineSegment(sketch, "E129.4.0.9", {"start": v(-38, 3.5) * mm, "end": v(-38, 6.6) * mm});
            skLineSegment(sketch, "E129.4.0.10", {"start": v(-42, 6.6) * mm, "end": v(-38, 6.6) * mm});
            skArc(sketch, "E129.4.0.11", {"start": v(-44, 9.6) * mm, "mid": v(-44.7, 9.3) * mm, "end": v(-45, 8.6) * mm});
            skArc(sketch, "E129.4.0.12", {"start": v(-35, 8.6) * mm, "mid": v(-35.3, 9.3) * mm, "end": v(-36, 9.6) * mm});
            skPoint(sketch, "E129.4.0.13", {"position": v(-40, 3) * mm});
            skLineSegment(sketch, "E129.4.0.14", {"start": v(-45, 8.6) * mm, "end": v(-45, 0) * mm});
            skLineSegment(sketch, "E129.4.0.15", {"start": v(-35, 0) * mm, "end": v(-35, 8.6) * mm});
            skLineSegment(sketch, "E129.direction1", {"start": v(35, 0) * mm, "end": v(15, 0) * mm, "construction": true});
            skLineSegment(sketch, "E130", {"start": v(35, 0) * mm, "end": v(25, 0) * mm});
            skLineSegment(sketch, "E131", {"start": v(15, 0) * mm, "end": v(5, 0) * mm});
            skLineSegment(sketch, "E132", {"start": v(-5, 0) * mm, "end": v(-15, 0) * mm});
            skLineSegment(sketch, "E133", {"start": v(-25, 0) * mm, "end": v(-35, 0) * mm});
            skLineSegment(sketch, "E134", {"start": v(0, -135) * mm, "end": v(0, -120) * mm, "construction": true});
            skLineSegment(sketch, "E135", {"start": v(-1.5, -120.02) * mm, "end": v(-1.5, -135.03) * mm});
            skLineSegment(sketch, "E136", {"start": v(1.5, -120.02) * mm, "end": v(1.5, -135.03) * mm});
            skSolve(sketch);
        }
        {
            var Q0;
            Q0=sQuery(id+"F2.wireOp",EDGE,"E136");
            cPlane(context, id + "F3", {"entities" : qUnion([Q0]), "cplaneType" : CPlaneType.LINE_ANGLE, "offset" : 25 * mm, "angle" : 0 * degree, "width" : 150 * mm, "height" : 150 * mm});
        }
        {
            var Q0;
            Q0=qCreatedBy(id+"F3.planeOp",FACE);
            var sketch = newSketch(context, id + "F4", { "sketchPlane" : qUnion([Q0])});
            skLineSegment(sketch, "E137.0", {"start": v(-465.45, -120.02) * mm, "end": v(-465.45, -135.03) * mm});
            skLineSegment(sketch, "E138", {"start": v(-465.45, -135.03) * mm, "end": v(-495.45, -135.03) * mm});
            skLineSegment(sketch, "E139", {"start": v(-495.45, -135.03) * mm, "end": v(-465.45, -57.25) * mm});
            skLineSegment(sketch, "E140", {"start": v(-465.45, -57.25) * mm, "end": v(-465.45, -120.02) * mm});
            skLineSegment(sketch, "E141", {"start": v(-435.45, -120.02) * mm, "end": v(-435.45, -135.03) * mm});
            skLineSegment(sketch, "E142", {"start": v(-435.45, -135.03) * mm, "end": v(-465.45, -135.03) * mm});
            skLineSegment(sketch, "E143", {"start": v(-435.45, -120.02) * mm, "end": v(-465.45, -120.02) * mm});
            skLineSegment(sketch, "E144", {"start": v(-468.45, -135.03) * mm, "end": v(-468.45, -65.03) * mm});
            skLineSegment(sketch, "E145", {"start": v(-465.45, -120.02) * mm, "end": v(-468.45, -120.02) * mm});
            skLineSegment(sketch, "E146", {"start": v(-481.15, -136.53) * mm, "end": v(-495.45, -136.53) * mm});
            skLineSegment(sketch, "E147", {"start": v(-495.45, -136.53) * mm, "end": v(-495.45, -135.03) * mm});
            skLineSegment(sketch, "E148", {"start": v(-480.45, -135.03) * mm, "end": v(-481.15, -136.53) * mm});
            skLineSegment(sketch, "E149", {"start": v(-494.68, -133.03) * mm, "end": v(-574.18, -133.03) * mm});
            skLineSegment(sketch, "E150", {"start": v(-574.68, -132.53) * mm, "end": v(-574.68, -131.53) * mm});
            skLineSegment(sketch, "E151", {"start": v(-574.18, -131.03) * mm, "end": v(-564.68, -131.03) * mm});
            skLineSegment(sketch, "E152", {"start": v(-564.68, -131.03) * mm, "end": v(-564.68, -127.03) * mm});
            skLineSegment(sketch, "E153", {"start": v(-564.68, -127.03) * mm, "end": v(-574.18, -127.03) * mm});
            skLineSegment(sketch, "E154", {"start": v(-574.68, -126.53) * mm, "end": v(-574.68, -125.53) * mm});
            skLineSegment(sketch, "E155", {"start": v(-574.18, -125.03) * mm, "end": v(-491.6, -125.03) * mm});
            skPoint(sketch, "E156.visualSharp", {"position": v(-574.68, -131.03) * mm});
            skArc(sketch, "E156.filletArc", {"start": v(-574.18, -131.03) * mm, "mid": v(-574.53, -131.17) * mm, "end": v(-574.68, -131.53) * mm});
            skPoint(sketch, "E157.visualSharp", {"position": v(-574.68, -127.03) * mm});
            skArc(sketch, "E157.filletArc", {"start": v(-574.68, -126.53) * mm, "mid": v(-574.53, -126.88) * mm, "end": v(-574.18, -127.03) * mm});
            skPoint(sketch, "E158.visualSharp", {"position": v(-574.68, -125.03) * mm});
            skArc(sketch, "E158.filletArc", {"start": v(-574.18, -125.03) * mm, "mid": v(-574.53, -125.17) * mm, "end": v(-574.68, -125.53) * mm});
            skPoint(sketch, "E159.visualSharp", {"position": v(-574.68, -133.03) * mm});
            skArc(sketch, "E159.filletArc", {"start": v(-574.68, -132.53) * mm, "mid": v(-574.53, -132.88) * mm, "end": v(-574.18, -133.03) * mm});
            skSolve(sketch);
        }
        {
            var Q0;
            {var subQ0=sQuery(id+"F2.wireOp",EDGE,"E126");Q0=makeQuery(id+"F2.imprint","IMPRINT",FACE,{"disambiguationData":[TD([[makeQuery(id+"F2.imprint","IMPRINT",EDGE,{"derivedFrom":subQ0}),-1.0]])]});}
            cPlane(context, id + "F5", {"entities" : qUnion([Q0]), "cplaneType" : CPlaneType.OFFSET, "offset" : 3 * mm, "width" : 150 * mm, "height" : 150 * mm});
        }
        {
            var Q0;
            Q0=qCreatedBy(id+"F5.planeOp",FACE);
            var sketch = newSketch(context, id + "F6", { "sketchPlane" : qUnion([Q0])});
            skCircle(sketch, "E160.0", {"center": v(0, -177) * mm, "radius": 57 * mm});
            skCircle(sketch, "E160.1", {"center": v(0, -177) * mm, "radius": 42 * mm});
            skLineSegment(sketch, "E161.0", {"start": v(42, -177) * mm, "end": v(57, -177) * mm});
            skLineSegment(sketch, "E162.0", {"start": v(-42, -177) * mm, "end": v(-57, -177) * mm});
            skLineSegment(sketch, "E163", {"start": v(49.5, -177) * mm, "end": v(49.5, -171) * mm, "construction": true});
            skCircle(sketch, "E164", {"center": v(49.5, -171) * mm, "radius": 2 * mm});
            skLineSegment(sketch, "E165", {"start": v(0, -177) * mm, "end": v(0, -152.27) * mm, "construction": true});
            skCircle(sketch, "E166.MirrorC", {"center": v(49.5, -183) * mm, "radius": 2 * mm});
            skCircle(sketch, "E167.MirrorC", {"center": v(-49.5, -183) * mm, "radius": 2 * mm});
            skCircle(sketch, "E168.MirrorC", {"center": v(-49.5, -171) * mm, "radius": 2 * mm});
            skLineSegment(sketch, "E169", {"start": v(0, -177) * mm, "end": v(55.06, -162.25) * mm});
            skLineSegment(sketch, "E170.MirrorCS", {"start": v(0, -177) * mm, "end": v(55.06, -191.75) * mm});
            skLineSegment(sketch, "E171.MirrorCS", {"start": v(0, -177) * mm, "end": v(-55.06, -162.25) * mm});
            skLineSegment(sketch, "E172.MirrorCS", {"start": v(0, -177) * mm, "end": v(-55.06, -191.75) * mm});
            skSolve(sketch);
        }
        {
            var Q0;
            {var subQ0=sQuery(id+"F0.wireOp",EDGE,"E110.0.5.0");Q0=makeQuery(id+"F0.imprint","IMPRINT",FACE,{"disambiguationData":[TD([[makeQuery(id+"F0.imprint","IMPRINT",EDGE,{"derivedFrom":subQ0}),-1.0]])]});}
            var Q1;
            {var subQ0=sQuery(id+"F0.wireOp",EDGE,"E110.0.5.2");Q1=makeQuery(id+"F0.imprint","IMPRINT",FACE,{"disambiguationData":[TD([[makeQuery(id+"F0.imprint","IMPRINT",EDGE,{"derivedFrom":subQ0}),-1.0]])]});}
            var Q2;
            {var subQ0=sQuery(id+"F0.wireOp",EDGE,"E110.0.5.4");Q2=makeQuery(id+"F0.imprint","IMPRINT",FACE,{"disambiguationData":[TD([[makeQuery(id+"F0.imprint","IMPRINT",EDGE,{"derivedFrom":subQ0}),-1.0]])]});}
            var Q3;
            {var subQ0=sQuery(id+"F0.wireOp",EDGE,"E110.0.5.6");Q3=makeQuery(id+"F0.imprint","IMPRINT",FACE,{"disambiguationData":[TD([[makeQuery(id+"F0.imprint","IMPRINT",EDGE,{"derivedFrom":subQ0}),-1.0]])]});}
            var Q4;
            {var subQ0=sQuery(id+"F0.wireOp",EDGE,"E110.0.5.8");Q4=makeQuery(id+"F0.imprint","IMPRINT",FACE,{"disambiguationData":[TD([[makeQuery(id+"F0.imprint","IMPRINT",EDGE,{"derivedFrom":subQ0}),-1.0]])]});}
            var Q5;
            {var subQ0=sQuery(id+"F0.wireOp",EDGE,"E110.0.5.10");Q5=makeQuery(id+"F0.imprint","IMPRINT",FACE,{"disambiguationData":[TD([[makeQuery(id+"F0.imprint","IMPRINT",EDGE,{"derivedFrom":subQ0}),-1.0]])]});}
            var Q6;
            Q6=makeQuery(id+"F0.imprint","IMPRINT",FACE,{"disambiguationData":[TD([[makeQuery(id+"F0.imprint","IMPRINT",EDGE,{"derivedFrom":sQuery(id+"F0.wireOp",EDGE,"E0.bottom")}),-1.0]])]});
            var Q7;
            {var subQ0=sQuery(id+"F0.wireOp",EDGE,"E110.0.6.0");Q7=makeQuery(id+"F0.imprint","IMPRINT",FACE,{"disambiguationData":[TD([[makeQuery(id+"F0.imprint","IMPRINT",EDGE,{"derivedFrom":subQ0}),-1.0]])]});}
            var Q8;
            {var subQ0=sQuery(id+"F0.wireOp",EDGE,"E110.0.6.2");Q8=makeQuery(id+"F0.imprint","IMPRINT",FACE,{"disambiguationData":[TD([[makeQuery(id+"F0.imprint","IMPRINT",EDGE,{"derivedFrom":subQ0}),-1.0]])]});}
            var Q9;
            {var subQ0=sQuery(id+"F0.wireOp",EDGE,"E110.0.6.4");Q9=makeQuery(id+"F0.imprint","IMPRINT",FACE,{"disambiguationData":[TD([[makeQuery(id+"F0.imprint","IMPRINT",EDGE,{"derivedFrom":subQ0}),-1.0]])]});}
            var Q10;
            {var subQ0=sQuery(id+"F0.wireOp",EDGE,"E110.0.6.6");Q10=makeQuery(id+"F0.imprint","IMPRINT",FACE,{"disambiguationData":[TD([[makeQuery(id+"F0.imprint","IMPRINT",EDGE,{"derivedFrom":subQ0}),-1.0]])]});}
            var Q11;
            {var subQ0=sQuery(id+"F0.wireOp",EDGE,"E110.0.6.8");Q11=makeQuery(id+"F0.imprint","IMPRINT",FACE,{"disambiguationData":[TD([[makeQuery(id+"F0.imprint","IMPRINT",EDGE,{"derivedFrom":subQ0}),-1.0]])]});}
            var Q12;
            {var subQ0=sQuery(id+"F0.wireOp",EDGE,"E110.0.6.10");Q12=makeQuery(id+"F0.imprint","IMPRINT",FACE,{"disambiguationData":[TD([[makeQuery(id+"F0.imprint","IMPRINT",EDGE,{"derivedFrom":subQ0}),-1.0]])]});}
            var Q13;
            {var subQ0=sQuery(id+"F0.wireOp",EDGE,"E110.0.7.0");Q13=makeQuery(id+"F0.imprint","IMPRINT",FACE,{"disambiguationData":[TD([[makeQuery(id+"F0.imprint","IMPRINT",EDGE,{"derivedFrom":subQ0}),-1.0]])]});}
            var Q14;
            {var subQ0=sQuery(id+"F0.wireOp",EDGE,"E110.0.7.2");Q14=makeQuery(id+"F0.imprint","IMPRINT",FACE,{"disambiguationData":[TD([[makeQuery(id+"F0.imprint","IMPRINT",EDGE,{"derivedFrom":subQ0}),-1.0]])]});}
            var Q15;
            {var subQ0=sQuery(id+"F0.wireOp",EDGE,"E110.0.7.4");Q15=makeQuery(id+"F0.imprint","IMPRINT",FACE,{"disambiguationData":[TD([[makeQuery(id+"F0.imprint","IMPRINT",EDGE,{"derivedFrom":subQ0}),-1.0]])]});}
            var Q16;
            {var subQ0=sQuery(id+"F0.wireOp",EDGE,"E110.0.7.8");Q16=makeQuery(id+"F0.imprint","IMPRINT",FACE,{"disambiguationData":[TD([[makeQuery(id+"F0.imprint","IMPRINT",EDGE,{"derivedFrom":subQ0}),-1.0]])]});}
            var Q17;
            {var subQ0=sQuery(id+"F0.wireOp",EDGE,"E110.0.7.10");Q17=makeQuery(id+"F0.imprint","IMPRINT",FACE,{"disambiguationData":[TD([[makeQuery(id+"F0.imprint","IMPRINT",EDGE,{"derivedFrom":subQ0}),-1.0]])]});}
            var Q18;
            {var subQ0=sQuery(id+"F0.wireOp",EDGE,"E110.0.7.6");Q18=makeQuery(id+"F0.imprint","IMPRINT",FACE,{"disambiguationData":[TD([[makeQuery(id+"F0.imprint","IMPRINT",EDGE,{"derivedFrom":subQ0}),-1.0]])]});}
            var Q19;
            {var subQ0=sQuery(id+"F0.wireOp",EDGE,"E110.0.4.0");Q19=makeQuery(id+"F0.imprint","IMPRINT",FACE,{"disambiguationData":[TD([[makeQuery(id+"F0.imprint","IMPRINT",EDGE,{"derivedFrom":subQ0}),-1.0]])]});}
            var Q20;
            {var subQ0=sQuery(id+"F0.wireOp",EDGE,"E110.0.4.2");Q20=makeQuery(id+"F0.imprint","IMPRINT",FACE,{"disambiguationData":[TD([[makeQuery(id+"F0.imprint","IMPRINT",EDGE,{"derivedFrom":subQ0}),-1.0]])]});}
            var Q21;
            {var subQ0=sQuery(id+"F0.wireOp",EDGE,"E110.0.4.4");Q21=makeQuery(id+"F0.imprint","IMPRINT",FACE,{"disambiguationData":[TD([[makeQuery(id+"F0.imprint","IMPRINT",EDGE,{"derivedFrom":subQ0}),-1.0]])]});}
            var Q22;
            {var subQ0=sQuery(id+"F0.wireOp",EDGE,"E110.0.4.6");Q22=makeQuery(id+"F0.imprint","IMPRINT",FACE,{"disambiguationData":[TD([[makeQuery(id+"F0.imprint","IMPRINT",EDGE,{"derivedFrom":subQ0}),-1.0]])]});}
            var Q23;
            {var subQ0=sQuery(id+"F0.wireOp",EDGE,"E110.0.4.8");Q23=makeQuery(id+"F0.imprint","IMPRINT",FACE,{"disambiguationData":[TD([[makeQuery(id+"F0.imprint","IMPRINT",EDGE,{"derivedFrom":subQ0}),-1.0]])]});}
            var Q24;
            {var subQ0=sQuery(id+"F0.wireOp",EDGE,"E110.0.4.10");Q24=makeQuery(id+"F0.imprint","IMPRINT",FACE,{"disambiguationData":[TD([[makeQuery(id+"F0.imprint","IMPRINT",EDGE,{"derivedFrom":subQ0}),-1.0]])]});}
            var Q25;
            {var subQ0=sQuery(id+"F0.wireOp",EDGE,"E110.0.3.0");Q25=makeQuery(id+"F0.imprint","IMPRINT",FACE,{"disambiguationData":[TD([[makeQuery(id+"F0.imprint","IMPRINT",EDGE,{"derivedFrom":subQ0}),-1.0]])]});}
            var Q26;
            {var subQ0=sQuery(id+"F0.wireOp",EDGE,"E110.0.3.2");Q26=makeQuery(id+"F0.imprint","IMPRINT",FACE,{"disambiguationData":[TD([[makeQuery(id+"F0.imprint","IMPRINT",EDGE,{"derivedFrom":subQ0}),-1.0]])]});}
            var Q27;
            {var subQ0=sQuery(id+"F0.wireOp",EDGE,"E110.0.3.4");Q27=makeQuery(id+"F0.imprint","IMPRINT",FACE,{"disambiguationData":[TD([[makeQuery(id+"F0.imprint","IMPRINT",EDGE,{"derivedFrom":subQ0}),-1.0]])]});}
            var Q28;
            {var subQ0=sQuery(id+"F0.wireOp",EDGE,"E110.0.3.6");Q28=makeQuery(id+"F0.imprint","IMPRINT",FACE,{"disambiguationData":[TD([[makeQuery(id+"F0.imprint","IMPRINT",EDGE,{"derivedFrom":subQ0}),-1.0]])]});}
            var Q29;
            {var subQ0=sQuery(id+"F0.wireOp",EDGE,"E110.0.3.8");Q29=makeQuery(id+"F0.imprint","IMPRINT",FACE,{"disambiguationData":[TD([[makeQuery(id+"F0.imprint","IMPRINT",EDGE,{"derivedFrom":subQ0}),-1.0]])]});}
            var Q30;
            {var subQ0=sQuery(id+"F0.wireOp",EDGE,"E110.0.3.10");Q30=makeQuery(id+"F0.imprint","IMPRINT",FACE,{"disambiguationData":[TD([[makeQuery(id+"F0.imprint","IMPRINT",EDGE,{"derivedFrom":subQ0}),-1.0]])]});}
            var Q31;
            {var subQ0=sQuery(id+"F0.wireOp",EDGE,"E110.0.2.0");Q31=makeQuery(id+"F0.imprint","IMPRINT",FACE,{"disambiguationData":[TD([[makeQuery(id+"F0.imprint","IMPRINT",EDGE,{"derivedFrom":subQ0}),-1.0]])]});}
            var Q32;
            {var subQ0=sQuery(id+"F0.wireOp",EDGE,"E110.0.2.2");Q32=makeQuery(id+"F0.imprint","IMPRINT",FACE,{"disambiguationData":[TD([[makeQuery(id+"F0.imprint","IMPRINT",EDGE,{"derivedFrom":subQ0}),-1.0]])]});}
            var Q33;
            {var subQ0=sQuery(id+"F0.wireOp",EDGE,"E110.0.2.4");Q33=makeQuery(id+"F0.imprint","IMPRINT",FACE,{"disambiguationData":[TD([[makeQuery(id+"F0.imprint","IMPRINT",EDGE,{"derivedFrom":subQ0}),-1.0]])]});}
            var Q34;
            {var subQ0=sQuery(id+"F0.wireOp",EDGE,"E110.0.2.6");Q34=makeQuery(id+"F0.imprint","IMPRINT",FACE,{"disambiguationData":[TD([[makeQuery(id+"F0.imprint","IMPRINT",EDGE,{"derivedFrom":subQ0}),-1.0]])]});}
            var Q35;
            {var subQ0=sQuery(id+"F0.wireOp",EDGE,"E110.0.2.8");Q35=makeQuery(id+"F0.imprint","IMPRINT",FACE,{"disambiguationData":[TD([[makeQuery(id+"F0.imprint","IMPRINT",EDGE,{"derivedFrom":subQ0}),-1.0]])]});}
            var Q36;
            {var subQ0=sQuery(id+"F0.wireOp",EDGE,"E110.0.2.10");Q36=makeQuery(id+"F0.imprint","IMPRINT",FACE,{"disambiguationData":[TD([[makeQuery(id+"F0.imprint","IMPRINT",EDGE,{"derivedFrom":subQ0}),-1.0]])]});}
            var Q37;
            {var subQ0=sQuery(id+"F0.wireOp",EDGE,"E110.0.1.0");Q37=makeQuery(id+"F0.imprint","IMPRINT",FACE,{"disambiguationData":[TD([[makeQuery(id+"F0.imprint","IMPRINT",EDGE,{"derivedFrom":subQ0}),-1.0]])]});}
            var Q38;
            {var subQ0=sQuery(id+"F0.wireOp",EDGE,"E110.0.1.2");Q38=makeQuery(id+"F0.imprint","IMPRINT",FACE,{"disambiguationData":[TD([[makeQuery(id+"F0.imprint","IMPRINT",EDGE,{"derivedFrom":subQ0}),-1.0]])]});}
            var Q39;
            {var subQ0=sQuery(id+"F0.wireOp",EDGE,"E110.0.1.4");Q39=makeQuery(id+"F0.imprint","IMPRINT",FACE,{"disambiguationData":[TD([[makeQuery(id+"F0.imprint","IMPRINT",EDGE,{"derivedFrom":subQ0}),-1.0]])]});}
            var Q40;
            {var subQ0=sQuery(id+"F0.wireOp",EDGE,"E110.0.1.6");Q40=makeQuery(id+"F0.imprint","IMPRINT",FACE,{"disambiguationData":[TD([[makeQuery(id+"F0.imprint","IMPRINT",EDGE,{"derivedFrom":subQ0}),-1.0]])]});}
            var Q41;
            {var subQ0=sQuery(id+"F0.wireOp",EDGE,"E110.0.1.8");Q41=makeQuery(id+"F0.imprint","IMPRINT",FACE,{"disambiguationData":[TD([[makeQuery(id+"F0.imprint","IMPRINT",EDGE,{"derivedFrom":subQ0}),-1.0]])]});}
            var Q42;
            {var subQ0=sQuery(id+"F0.wireOp",EDGE,"E110.0.1.10");Q42=makeQuery(id+"F0.imprint","IMPRINT",FACE,{"disambiguationData":[TD([[makeQuery(id+"F0.imprint","IMPRINT",EDGE,{"derivedFrom":subQ0}),-1.0]])]});}
            var Q43;
            {var subQ0=sQuery(id+"F0.wireOp",EDGE,"E98");Q43=makeQuery(id+"F0.imprint","IMPRINT",FACE,{"disambiguationData":[TD([[makeQuery(id+"F0.imprint","IMPRINT",EDGE,{"derivedFrom":subQ0}),-1.0]])]});}
            var Q44;
            {var subQ0=sQuery(id+"F0.wireOp",EDGE,"E99");Q44=makeQuery(id+"F0.imprint","IMPRINT",FACE,{"disambiguationData":[TD([[makeQuery(id+"F0.imprint","IMPRINT",EDGE,{"derivedFrom":subQ0}),-1.0]])]});}
            var Q45;
            {var subQ0=sQuery(id+"F0.wireOp",EDGE,"E100");Q45=makeQuery(id+"F0.imprint","IMPRINT",FACE,{"disambiguationData":[TD([[makeQuery(id+"F0.imprint","IMPRINT",EDGE,{"derivedFrom":subQ0}),-1.0]])]});}
            var Q46;
            {var subQ0=sQuery(id+"F0.wireOp",EDGE,"E101");Q46=makeQuery(id+"F0.imprint","IMPRINT",FACE,{"disambiguationData":[TD([[makeQuery(id+"F0.imprint","IMPRINT",EDGE,{"derivedFrom":subQ0}),-1.0]])]});}
            var Q47;
            {var subQ0=sQuery(id+"F0.wireOp",EDGE,"E102");Q47=makeQuery(id+"F0.imprint","IMPRINT",FACE,{"disambiguationData":[TD([[makeQuery(id+"F0.imprint","IMPRINT",EDGE,{"derivedFrom":subQ0}),-1.0]])]});}
            var Q48;
            {var subQ0=sQuery(id+"F0.wireOp",EDGE,"E103");Q48=makeQuery(id+"F0.imprint","IMPRINT",FACE,{"disambiguationData":[TD([[makeQuery(id+"F0.imprint","IMPRINT",EDGE,{"derivedFrom":subQ0}),-1.0]])]});}
            extrude(context, id + "F7", {"entities" : qUnion([Q0, Q1, Q2, Q3, Q4, Q5, Q6, Q7, Q8, Q9, Q10, Q11, Q12, Q13, Q14, Q15, Q16, Q17, Q18, Q19, Q20, Q21, Q22, Q23, Q24, Q25, Q26, Q27, Q28, Q29, Q30, Q31, Q32, Q33, Q34, Q35, Q36, Q37, Q38, Q39, Q40, Q41, Q42, Q43, Q44, Q45, Q46, Q47, Q48]), "depth" : 3 * mm});
        }
        {
            var Q0;
            Q0=makeQuery(id+"F2.imprint","IMPRINT",FACE,{"disambiguationData":[TD([[makeQuery(id+"F2.imprint","IMPRINT",EDGE,{"derivedFrom":sQuery(id+"F2.wireOp",EDGE,"E116")}),1.0]])]});
            var Q1;
            {var subQ4=sQuery(id+"F2.wireOp",EDGE,"E126");Q1=makeQuery(id+"F2.imprint","IMPRINT",FACE,{"disambiguationData":[TD([[makeQuery(id+"F2.imprint","IMPRINT",EDGE,{"derivedFrom":subQ4}),1.0]])]});}
            var Q2;
            {var subQ0=sQuery(id+"F2.wireOp",EDGE,"E127");Q2=makeQuery(id+"F2.imprint","IMPRINT",FACE,{"disambiguationData":[TD([[makeQuery(id+"F2.imprint","IMPRINT",EDGE,{"derivedFrom":subQ0}),-1.0]])]});}
            extrude(context, id + "F8", {"entities" : qUnion([Q0, Q1, Q2]), "depth" : 3 * mm});
        }
        {
            var Q0;
            {var subQ0=sQuery(id+"F4.wireOp",EDGE,"E139");var subQ1=sQuery(id+"F4.wireOp",EDGE,"E138");var subQ2=makeQuery(id+"F4.imprint","INTERSECT",VERTEX,{"derivedFrom":[subQ1,subQ0]});Q0=makeQuery(id+"F4.imprint","IMPRINT",FACE,{"disambiguationData":[TD([[makeQuery(id+"F4.imprint","IMPRINT",EDGE,{"disambiguationData":[TD([[subQ2,1.0]])],"derivedFrom":subQ1}),-1.0]])]});}
            var Q1;
            {var subQ0=sQuery(id+"F4.wireOp",EDGE,"E137.0");Q1=makeQuery(id+"F4.imprint","IMPRINT",FACE,{"disambiguationData":[TD([[makeQuery(id+"F4.imprint","IMPRINT",EDGE,{"derivedFrom":subQ0}),-1.0]])]});}
            var Q2;
            Q2=makeQuery(id+"F4.imprint","IMPRINT",FACE,{"disambiguationData":[TD([[makeQuery(id+"F4.imprint","IMPRINT",EDGE,{"derivedFrom":sQuery(id+"F4.wireOp",EDGE,"E137.0")}),1.0]])]});
            var Q3;
            Q3=makeQuery(id+"F4.imprint","IMPRINT",FACE,{"disambiguationData":[TD([[makeQuery(id+"F4.imprint","IMPRINT",EDGE,{"derivedFrom":sQuery(id+"F4.wireOp",EDGE,"E146")}),-1.0]])]});
            var Q4;
            {var subQ0=sQuery(id+"F4.wireOp",EDGE,"E149");Q4=makeQuery(id+"F4.imprint","IMPRINT",FACE,{"disambiguationData":[TD([[makeQuery(id+"F4.imprint","IMPRINT",EDGE,{"derivedFrom":subQ0}),-1.0]])]});}
            extrude(context, id + "F9", {"entities" : qUnion([Q0, Q1, Q2, Q3, Q4]), "oppositeDirection" : true, "depth" : 3 * mm});
        }
        {
            var Q0;
            {var subQ0=sQuery(id+"F2.wireOp",EDGE,"E126");Q0=makeQuery(id+"F2.imprint","IMPRINT",FACE,{"disambiguationData":[TD([[makeQuery(id+"F2.imprint","IMPRINT",EDGE,{"derivedFrom":subQ0}),-1.0]])]});}
            extrude(context, id + "F10", {"entities" : qUnion([Q0]), "depth" : 3 * mm});
        }
        {
            var Q0;
            Q0=makeQuery(id+"F6.imprint","IMPRINT",FACE,{"disambiguationData":[TD([[makeQuery(id+"F6.imprint","IMPRINT",EDGE,{"derivedFrom":sQuery(id+"F6.wireOp",EDGE,"E164")}),1.0]])]});
            var Q1;
            Q1=makeQuery(id+"F6.imprint","IMPRINT",FACE,{"disambiguationData":[TD([[makeQuery(id+"F6.imprint","IMPRINT",EDGE,{"derivedFrom":sQuery(id+"F6.wireOp",EDGE,"E166.MirrorC")}),-1.0]])]});
            var Q2;
            Q2=makeQuery(id+"F6.imprint","IMPRINT",FACE,{"disambiguationData":[TD([[makeQuery(id+"F6.imprint","IMPRINT",EDGE,{"derivedFrom":sQuery(id+"F6.wireOp",EDGE,"E168.MirrorC")}),-1.0]])]});
            var Q3;
            Q3=makeQuery(id+"F6.imprint","IMPRINT",FACE,{"disambiguationData":[TD([[makeQuery(id+"F6.imprint","IMPRINT",EDGE,{"derivedFrom":sQuery(id+"F6.wireOp",EDGE,"E167.MirrorC")}),1.0]])]});
            extrude(context, id + "F11", {"entities" : qUnion([Q0, Q1, Q2, Q3]), "operationType" : NewBodyOperationType.REMOVE, "oppositeDirection" : true, "depth" : 25 * mm});
        }
        {
            var Q0;
            {var subQ0=sQuery(id+"F6.wireOp",EDGE,"E161.0");Q0=makeQuery(id+"F6.imprint","IMPRINT",FACE,{"disambiguationData":[TD([[makeQuery(id+"F6.imprint","IMPRINT",EDGE,{"derivedFrom":subQ0}),1.0]])]});}
            var Q1;
            {var subQ0=sQuery(id+"F6.wireOp",EDGE,"E161.0");Q1=makeQuery(id+"F6.imprint","IMPRINT",FACE,{"disambiguationData":[TD([[makeQuery(id+"F6.imprint","IMPRINT",EDGE,{"derivedFrom":subQ0}),-1.0]])]});}
            var Q2;
            {var subQ0=sQuery(id+"F6.wireOp",EDGE,"E162.0");Q2=makeQuery(id+"F6.imprint","IMPRINT",FACE,{"disambiguationData":[TD([[makeQuery(id+"F6.imprint","IMPRINT",EDGE,{"derivedFrom":subQ0}),-1.0]])]});}
            var Q3;
            {var subQ0=sQuery(id+"F6.wireOp",EDGE,"E162.0");Q3=makeQuery(id+"F6.imprint","IMPRINT",FACE,{"disambiguationData":[TD([[makeQuery(id+"F6.imprint","IMPRINT",EDGE,{"derivedFrom":subQ0}),1.0]])]});}
            extrude(context, id + "F12", {"entities" : qUnion([Q0, Q1, Q2, Q3]), "depth" : 3 * mm});
        }
    });
